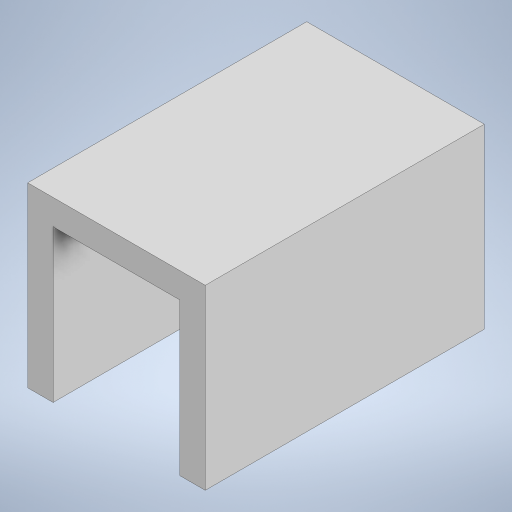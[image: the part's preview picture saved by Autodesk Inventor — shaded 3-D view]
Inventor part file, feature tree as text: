
AUTODESK INVENTOR PART (.ipt)
format: ipt  version: 2023 (Build 270158000, 158)  size: 179,712 bytes
history: native  units: in
note: dims shown in document units (in); Inventor stores cm internally (conversion verified against a paired STEP export)
features: extrude x3, sketch x3
ambient origin geometry x8: Origin, YZ Plane, XZ Plane, XY Plane, X Axis, Y Axis, Z Axis, Center Point
bodies: Solid1 (feature_tree)
feature tree (6):
  extrude  "Extrusion1"  Depth=0.5512in
  extrude  "Extrusion2"  Depth=0.3937in
  extrude  "Extrusion4"  Depth=0.7874in TaperAngle=0.0deg
  sketch  "Sketch1"  dims[d0=0.5512in d1=0.5512in]
  sketch  "Sketch2"  dims[d2=0.8661in d3=0.0in d4=0.3937in]
  sketch  "Sketch5"  dims[d5=0.7874in d6=0.7874in d7=0.0in d11=0.1969in d12=0.7874in d13=0.0787in d14=0.0in]
